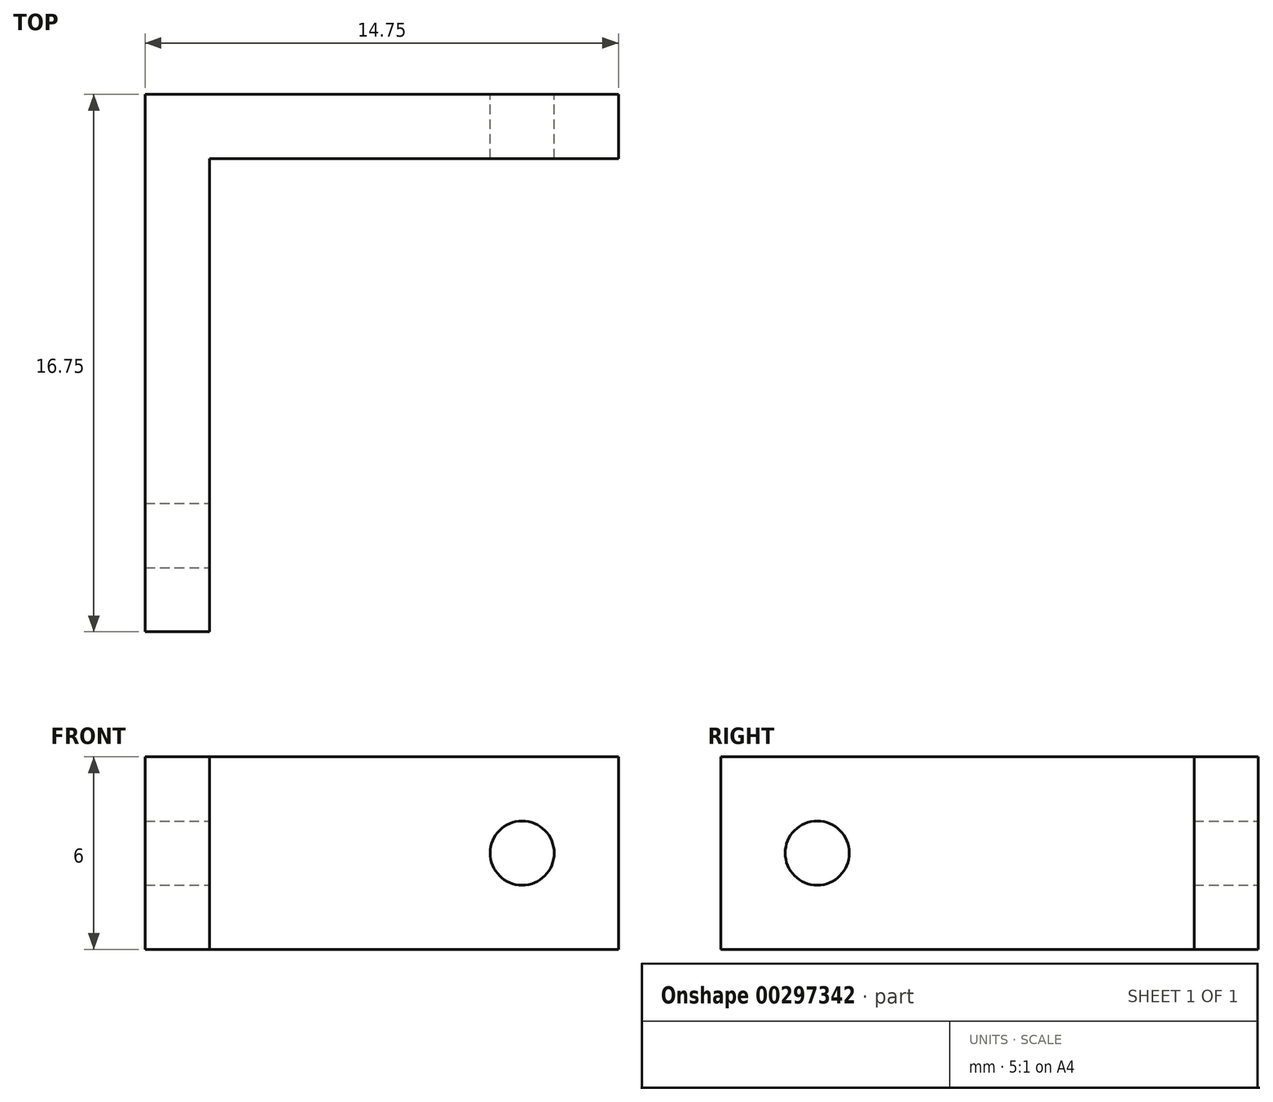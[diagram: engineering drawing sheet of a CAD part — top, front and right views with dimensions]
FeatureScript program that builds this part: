
annotation { "Feature Type Name" : "Feature", "Feature Type Description" : "" }
export const myFeature = defineFeature(function(context is Context, id is Id, definition is map)
    precondition{}
    {
        {
            var Q0;
            Q0=qCreatedBy(makeId("Front.planeOp"),FACE);
            var sketch = newSketch(context, id + "F0", { "sketchPlane" : qUnion([Q0])});
            skLineSegment(sketch, "E0.bottom", {"start": v(0, 0) * mm, "end": v(14.75, 0) * mm});
            skLineSegment(sketch, "E0.top", {"start": v(0, 6) * mm, "end": v(14.75, 6) * mm});
            skLineSegment(sketch, "E0.left", {"start": v(0, 0) * mm, "end": v(0, 6) * mm});
            skLineSegment(sketch, "E0.right", {"start": v(14.75, 0) * mm, "end": v(14.75, 6) * mm});
            skCircle(sketch, "E1", {"center": v(11.75, 3) * mm, "radius": 1 * mm});
            skSolve(sketch);
        }
        {
            var Q0;
            Q0 = qSketchRegion(id + "F0", true);
            extrude(context, id + "F1", {"entities" : qUnion([Q0]), "depth" : 2 * mm});
        }
        {
            var Q0;
            Q0=makeQuery(id+"F1.opExtrude","CAP_FACE",FACE,{"disambiguationData":[OSD([sQuery(id+"F0.wireOp",EDGE,"E0.bottom"),sQuery(id+"F0.wireOp",EDGE,"E0.top"),sQuery(id+"F0.wireOp",EDGE,"E0.left"),sQuery(id+"F0.wireOp",EDGE,"E0.right"),sQuery(id+"F0.wireOp",EDGE,"E1")])],"isStart":false});
            var sketch = newSketch(context, id + "F2", { "sketchPlane" : qUnion([Q0])});
            skLineSegment(sketch, "E2.bottom", {"start": v(0, 0) * mm, "end": v(2, 0) * mm});
            skLineSegment(sketch, "E2.top", {"start": v(0, 6) * mm, "end": v(2, 6) * mm});
            skLineSegment(sketch, "E2.left", {"start": v(0, 0) * mm, "end": v(0, 6) * mm});
            skLineSegment(sketch, "E2.right", {"start": v(2, 0) * mm, "end": v(2, 6) * mm});
            skSolve(sketch);
        }
        {
            var Q0;
            Q0 = qSketchRegion(id + "F2", true);
            extrude(context, id + "F3", {"entities" : qUnion([Q0]), "operationType" : NewBodyOperationType.ADD, "depth" : 14.75 * mm});
        }
        {
            var Q0;
            Q0=makeQuery(id+"F3.opExtrude","SWEPT_FACE",FACE,{"disambiguationData":[OSD([sQuery(id+"F2.wireOp",EDGE,"E2.right")])]});
            var sketch = newSketch(context, id + "F4", { "sketchPlane" : qUnion([Q0])});
            skCircle(sketch, "E3", {"center": v(-13.75, 3) * mm, "radius": 1 * mm});
            skSolve(sketch);
        }
        {
            var Q0;
            Q0 = qSketchRegion(id + "F4", true);
            extrude(context, id + "F5", {"entities" : qUnion([Q0]), "operationType" : NewBodyOperationType.REMOVE, "oppositeDirection" : true, "depth" : 25 * mm});
        }
    });
